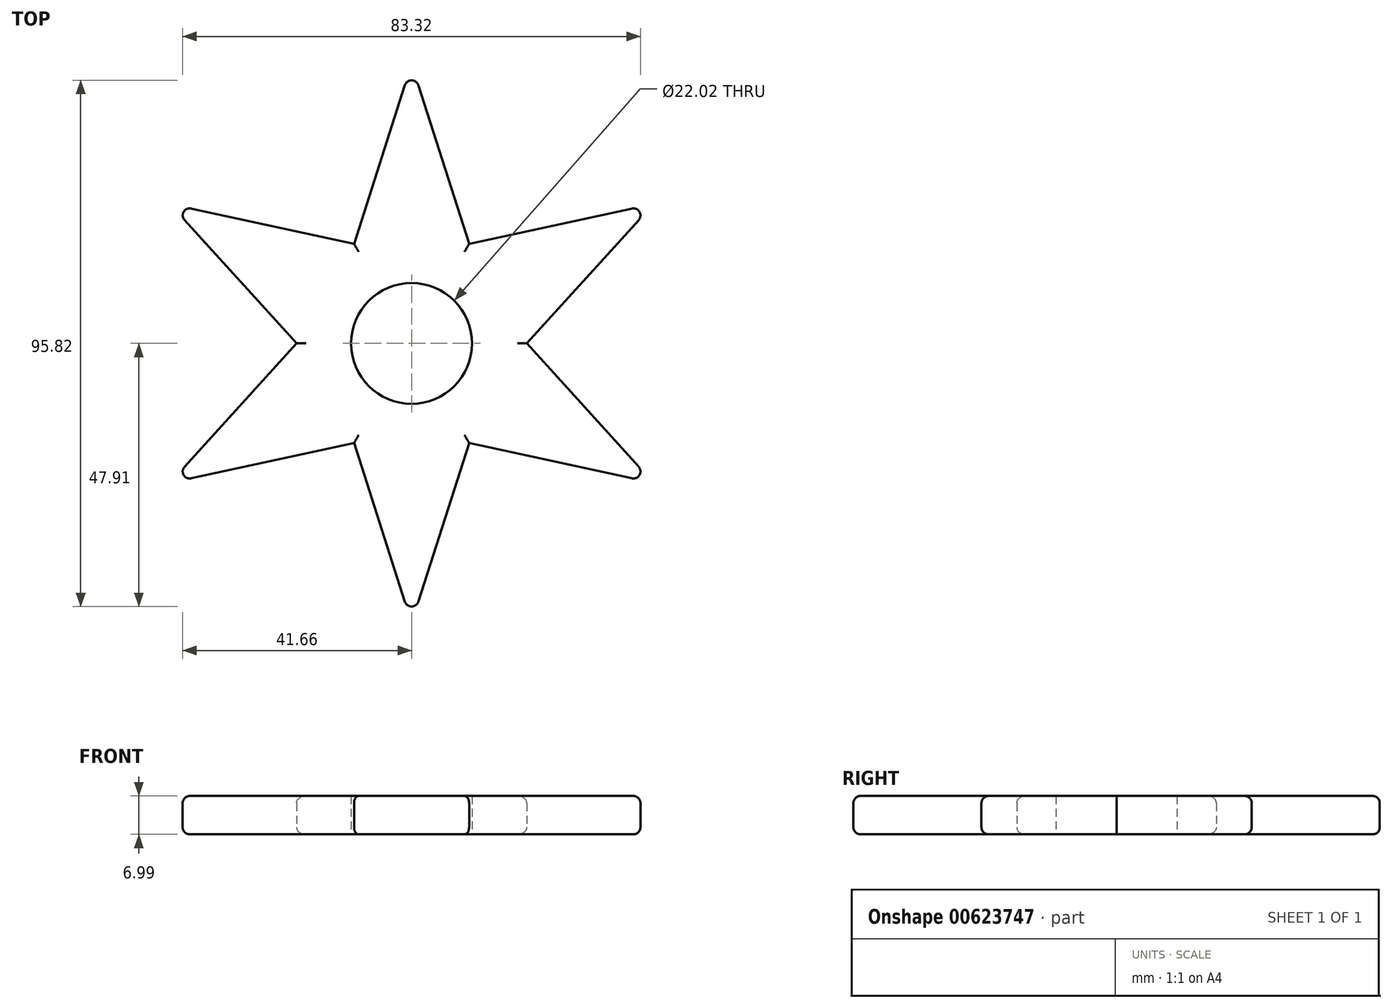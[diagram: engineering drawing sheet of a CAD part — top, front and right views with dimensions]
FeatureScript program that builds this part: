
annotation { "Feature Type Name" : "Feature", "Feature Type Description" : "" }
export const myFeature = defineFeature(function(context is Context, id is Id, definition is map)
    precondition{}
    {
        {
            var Q0;
            Q0=qCreatedBy(makeId("Top.planeOp"),FACE);
            var sketch = newSketch(context, id + "F0", { "sketchPlane" : qUnion([Q0])});
            skCircle(sketch, "E0", {"center": v(0, 0) * mm, "radius": 11.01 * mm});
            skLineSegment(sketch, "E1", {"start": v(0, 0) * mm, "end": v(0, 15.88) * mm});
            skLineSegment(sketch, "E2", {"start": v(0, 0) * mm, "end": v(13.75, -7.94) * mm});
            skLineSegment(sketch, "E3", {"start": v(0, 0) * mm, "end": v(-13.75, -7.94) * mm});
            skLineSegment(sketch, "E4", {"start": v(0, 0) * mm, "end": v(13.75, 7.94) * mm});
            skLineSegment(sketch, "E5", {"start": v(0, 0) * mm, "end": v(-13.75, 7.94) * mm});
            skLineSegment(sketch, "E6", {"start": v(0, 0) * mm, "end": v(0, -15.88) * mm});
            skLineSegment(sketch, "E7", {"start": v(10.48, 18.15) * mm, "end": v(44, 25.4) * mm});
            skLineSegment(sketch, "E8", {"start": v(20.96, 0) * mm, "end": v(44, 25.4) * mm});
            skLineSegment(sketch, "E9", {"start": v(20.96, 0) * mm, "end": v(44, -25.4) * mm});
            skLineSegment(sketch, "E10", {"start": v(10.48, -18.15) * mm, "end": v(44, -25.4) * mm});
            skLineSegment(sketch, "E11", {"start": v(-44, -25.4) * mm, "end": v(-10.48, -18.15) * mm});
            skLineSegment(sketch, "E12", {"start": v(-44, -25.4) * mm, "end": v(-20.96, 0) * mm});
            skLineSegment(sketch, "E13", {"start": v(-20.96, 0) * mm, "end": v(-44, 25.4) * mm});
            skLineSegment(sketch, "E14", {"start": v(-10.48, 18.15) * mm, "end": v(-44, 25.4) * mm});
            skLineSegment(sketch, "E15", {"start": v(10.48, 18.15) * mm, "end": v(0, 50.8) * mm});
            skLineSegment(sketch, "E16", {"start": v(-10.48, 18.15) * mm, "end": v(0, 50.8) * mm});
            skLineSegment(sketch, "E17", {"start": v(10.48, -18.15) * mm, "end": v(0, -50.8) * mm});
            skLineSegment(sketch, "E18", {"start": v(-10.48, -18.15) * mm, "end": v(0, -50.8) * mm});
            skCircle(sketch, "E19", {"center": v(0, 0) * mm, "radius": 15.88 * mm});
            skLineSegment(sketch, "E20", {"start": v(-44, 25.4) * mm, "end": v(0, 0) * mm});
            skLineSegment(sketch, "E21", {"start": v(0, 0) * mm, "end": v(0, 50.8) * mm});
            skLineSegment(sketch, "E22", {"start": v(44, 25.4) * mm, "end": v(0, 0) * mm});
            skLineSegment(sketch, "E23", {"start": v(44, -25.4) * mm, "end": v(0, 0) * mm});
            skLineSegment(sketch, "E24", {"start": v(0, 0) * mm, "end": v(0, -50.8) * mm});
            skLineSegment(sketch, "E25", {"start": v(0, 0) * mm, "end": v(-44, -25.4) * mm});
            skLineSegment(sketch, "E26", {"start": v(-20.96, 0) * mm, "end": v(-10.48, 18.15) * mm});
            skLineSegment(sketch, "E27", {"start": v(-10.48, 18.15) * mm, "end": v(10.48, 18.15) * mm});
            skLineSegment(sketch, "E28", {"start": v(10.48, 18.15) * mm, "end": v(20.96, 0) * mm});
            skLineSegment(sketch, "E29", {"start": v(20.96, 0) * mm, "end": v(10.48, -18.15) * mm});
            skLineSegment(sketch, "E30", {"start": v(10.48, -18.15) * mm, "end": v(-10.48, -18.15) * mm});
            skLineSegment(sketch, "E31", {"start": v(-10.48, -18.15) * mm, "end": v(-20.96, 0) * mm});
            skPoint(sketch, "E32", {"position": v(-15.72, 9.07) * mm});
            skPoint(sketch, "E33", {"position": v(0, 18.15) * mm});
            skPoint(sketch, "E34", {"position": v(15.72, 9.07) * mm});
            skPoint(sketch, "E35", {"position": v(15.72, -9.07) * mm});
            skPoint(sketch, "E36", {"position": v(0, -18.15) * mm});
            skPoint(sketch, "E37", {"position": v(-15.72, -9.07) * mm});
            skSolve(sketch);
        }
        {
            var Q0;
            Q0 = qSketchRegion(id + "F0", true);
            var Q1;
            {var subQ0=sQuery(id+"F0.wireOp",EDGE,"E1");var subQ1=sQuery(id+"F0.wireOp",EDGE,"E0");var subQ2=makeQuery(id+"F0.imprint","INTERSECT",VERTEX,{"derivedFrom":[subQ1,subQ0]});Q1=makeQuery(id+"F0.imprint","IMPRINT",FACE,{"disambiguationData":[TD([[makeQuery(id+"F0.imprint","IMPRINT",EDGE,{"disambiguationData":[TD([[subQ2,-1.0]])],"derivedFrom":subQ1}),-1.0]])]});}
            var Q2;
            {var subQ0=sQuery(id+"F0.wireOp",EDGE,"E1");var subQ1=sQuery(id+"F0.wireOp",EDGE,"E0");var subQ2=makeQuery(id+"F0.imprint","INTERSECT",VERTEX,{"derivedFrom":[subQ1,subQ0]});Q2=makeQuery(id+"F0.imprint","IMPRINT",FACE,{"disambiguationData":[TD([[makeQuery(id+"F0.imprint","IMPRINT",EDGE,{"disambiguationData":[TD([[subQ2,1.0]])],"derivedFrom":subQ1}),-1.0]])]});}
            var Q3;
            {var subQ0=sQuery(id+"F0.wireOp",EDGE,"E4");var subQ1=sQuery(id+"F0.wireOp",EDGE,"E0");var subQ2=makeQuery(id+"F0.imprint","INTERSECT",VERTEX,{"derivedFrom":[subQ1,subQ0]});Q3=makeQuery(id+"F0.imprint","IMPRINT",FACE,{"disambiguationData":[TD([[makeQuery(id+"F0.imprint","IMPRINT",EDGE,{"disambiguationData":[TD([[subQ2,1.0]])],"derivedFrom":subQ1}),-1.0]])]});}
            var Q4;
            {var subQ0=sQuery(id+"F0.wireOp",EDGE,"E6");var subQ1=sQuery(id+"F0.wireOp",EDGE,"E0");var subQ2=makeQuery(id+"F0.imprint","INTERSECT",VERTEX,{"derivedFrom":[subQ1,subQ0]});Q4=makeQuery(id+"F0.imprint","IMPRINT",FACE,{"disambiguationData":[TD([[makeQuery(id+"F0.imprint","IMPRINT",EDGE,{"disambiguationData":[TD([[subQ2,-1.0]])],"derivedFrom":subQ1}),-1.0]])]});}
            var Q5;
            {var subQ0=sQuery(id+"F0.wireOp",EDGE,"E3");var subQ1=sQuery(id+"F0.wireOp",EDGE,"E0");var subQ2=makeQuery(id+"F0.imprint","INTERSECT",VERTEX,{"derivedFrom":[subQ1,subQ0]});Q5=makeQuery(id+"F0.imprint","IMPRINT",FACE,{"disambiguationData":[TD([[makeQuery(id+"F0.imprint","IMPRINT",EDGE,{"disambiguationData":[TD([[subQ2,-1.0]])],"derivedFrom":subQ1}),-1.0]])]});}
            var Q6;
            {var subQ0=sQuery(id+"F0.wireOp",EDGE,"E5");var subQ1=sQuery(id+"F0.wireOp",EDGE,"E0");var subQ2=makeQuery(id+"F0.imprint","INTERSECT",VERTEX,{"derivedFrom":[subQ1,subQ0]});Q6=makeQuery(id+"F0.imprint","IMPRINT",FACE,{"disambiguationData":[TD([[makeQuery(id+"F0.imprint","IMPRINT",EDGE,{"disambiguationData":[TD([[subQ2,-1.0]])],"derivedFrom":subQ1}),-1.0]])]});}
            extrude(context, id + "F1", {"entities" : qUnion([Q0, Q1, Q2, Q3, Q4, Q5, Q6]), "depth" : 7 * mm, "offsetDistance" : 25.4 * mm});
        }
        {
            var Q0;
            Q0=makeQuery(id+"F1.opExtrude","SWEPT_EDGE",EDGE,{"disambiguationData":[OSD([sQuery(id+"F0.wireOp",EDGE,"E15"),sQuery(id+"F0.wireOp",EDGE,"E16"),sQuery(id+"F0.wireOp",EDGE,"E21")])]});
            var Q1;
            Q1=makeQuery(id+"F1.opExtrude","SWEPT_EDGE",EDGE,{"disambiguationData":[OSD([sQuery(id+"F0.wireOp",EDGE,"E11"),sQuery(id+"F0.wireOp",EDGE,"E12"),sQuery(id+"F0.wireOp",EDGE,"E25")])]});
            var Q2;
            Q2=makeQuery(id+"F1.opExtrude","SWEPT_EDGE",EDGE,{"disambiguationData":[OSD([sQuery(id+"F0.wireOp",EDGE,"E13"),sQuery(id+"F0.wireOp",EDGE,"E14"),sQuery(id+"F0.wireOp",EDGE,"E20")])]});
            var Q3;
            Q3=makeQuery(id+"F1.opExtrude","SWEPT_EDGE",EDGE,{"disambiguationData":[OSD([sQuery(id+"F0.wireOp",EDGE,"E17"),sQuery(id+"F0.wireOp",EDGE,"E18"),sQuery(id+"F0.wireOp",EDGE,"E24")])]});
            var Q4;
            Q4=makeQuery(id+"F1.opExtrude","SWEPT_EDGE",EDGE,{"disambiguationData":[OSD([sQuery(id+"F0.wireOp",EDGE,"E9"),sQuery(id+"F0.wireOp",EDGE,"E10"),sQuery(id+"F0.wireOp",EDGE,"E23")])]});
            var Q5;
            Q5=makeQuery(id+"F1.opExtrude","SWEPT_EDGE",EDGE,{"disambiguationData":[OSD([sQuery(id+"F0.wireOp",EDGE,"E7"),sQuery(id+"F0.wireOp",EDGE,"E8"),sQuery(id+"F0.wireOp",EDGE,"E22")])]});
            fillet(context, id + "F2", {"entities" : qUnion([Q0, Q1, Q2, Q3, Q4, Q5]), "radius" : 1.27 * mm, "tangentPropagation" : true, "allowEdgeOverflow" : false});
        }
        {
            var Q0;
            Q0=makeQuery(id+"F1.opExtrude","CAP_EDGE",EDGE,{"disambiguationData":[OSD([sQuery(id+"F0.wireOp",EDGE,"E9")])],"isStart":false});
            var Q1;
            Q1=makeQuery(id+"F1.opExtrude","CAP_EDGE",EDGE,{"disambiguationData":[OSD([sQuery(id+"F0.wireOp",EDGE,"E17")])],"isStart":false});
            var Q2;
            Q2=makeQuery(id+"F1.opExtrude","CAP_EDGE",EDGE,{"disambiguationData":[OSD([sQuery(id+"F0.wireOp",EDGE,"E11")])],"isStart":false});
            var Q3;
            Q3=makeQuery(id+"F1.opExtrude","CAP_EDGE",EDGE,{"disambiguationData":[OSD([sQuery(id+"F0.wireOp",EDGE,"E13")])],"isStart":false});
            var Q4;
            Q4=makeQuery(id+"F1.opExtrude","CAP_EDGE",EDGE,{"disambiguationData":[OSD([sQuery(id+"F0.wireOp",EDGE,"E7")])],"isStart":false});
            var Q5;
            Q5=makeQuery(id+"F1.opExtrude","CAP_EDGE",EDGE,{"disambiguationData":[OSD([sQuery(id+"F0.wireOp",EDGE,"E16")])],"isStart":false});
            var Q6;
            Q6=makeQuery(id+"F1.opExtrude","CAP_EDGE",EDGE,{"disambiguationData":[OSD([sQuery(id+"F0.wireOp",EDGE,"E7")])],"isStart":true});
            var Q7;
            Q7=makeQuery(id+"F1.opExtrude","CAP_EDGE",EDGE,{"disambiguationData":[OSD([sQuery(id+"F0.wireOp",EDGE,"E10")])],"isStart":true});
            var Q8;
            Q8=makeQuery(id+"F1.opExtrude","CAP_EDGE",EDGE,{"disambiguationData":[OSD([sQuery(id+"F0.wireOp",EDGE,"E17")])],"isStart":true});
            var Q9;
            Q9=makeQuery(id+"F1.opExtrude","CAP_EDGE",EDGE,{"disambiguationData":[OSD([sQuery(id+"F0.wireOp",EDGE,"E11")])],"isStart":true});
            var Q10;
            Q10=makeQuery(id+"F1.opExtrude","CAP_EDGE",EDGE,{"disambiguationData":[OSD([sQuery(id+"F0.wireOp",EDGE,"E13")])],"isStart":true});
            var Q11;
            Q11=makeQuery(id+"F1.opExtrude","CAP_EDGE",EDGE,{"disambiguationData":[OSD([sQuery(id+"F0.wireOp",EDGE,"E15")])],"isStart":true});
            fillet(context, id + "F3", {"entities" : qUnion([Q0, Q1, Q2, Q3, Q4, Q5, Q6, Q7, Q8, Q9, Q10, Q11]), "radius" : 1.27 * mm, "tangentPropagation" : true, "allowEdgeOverflow" : false});
        }
    });
